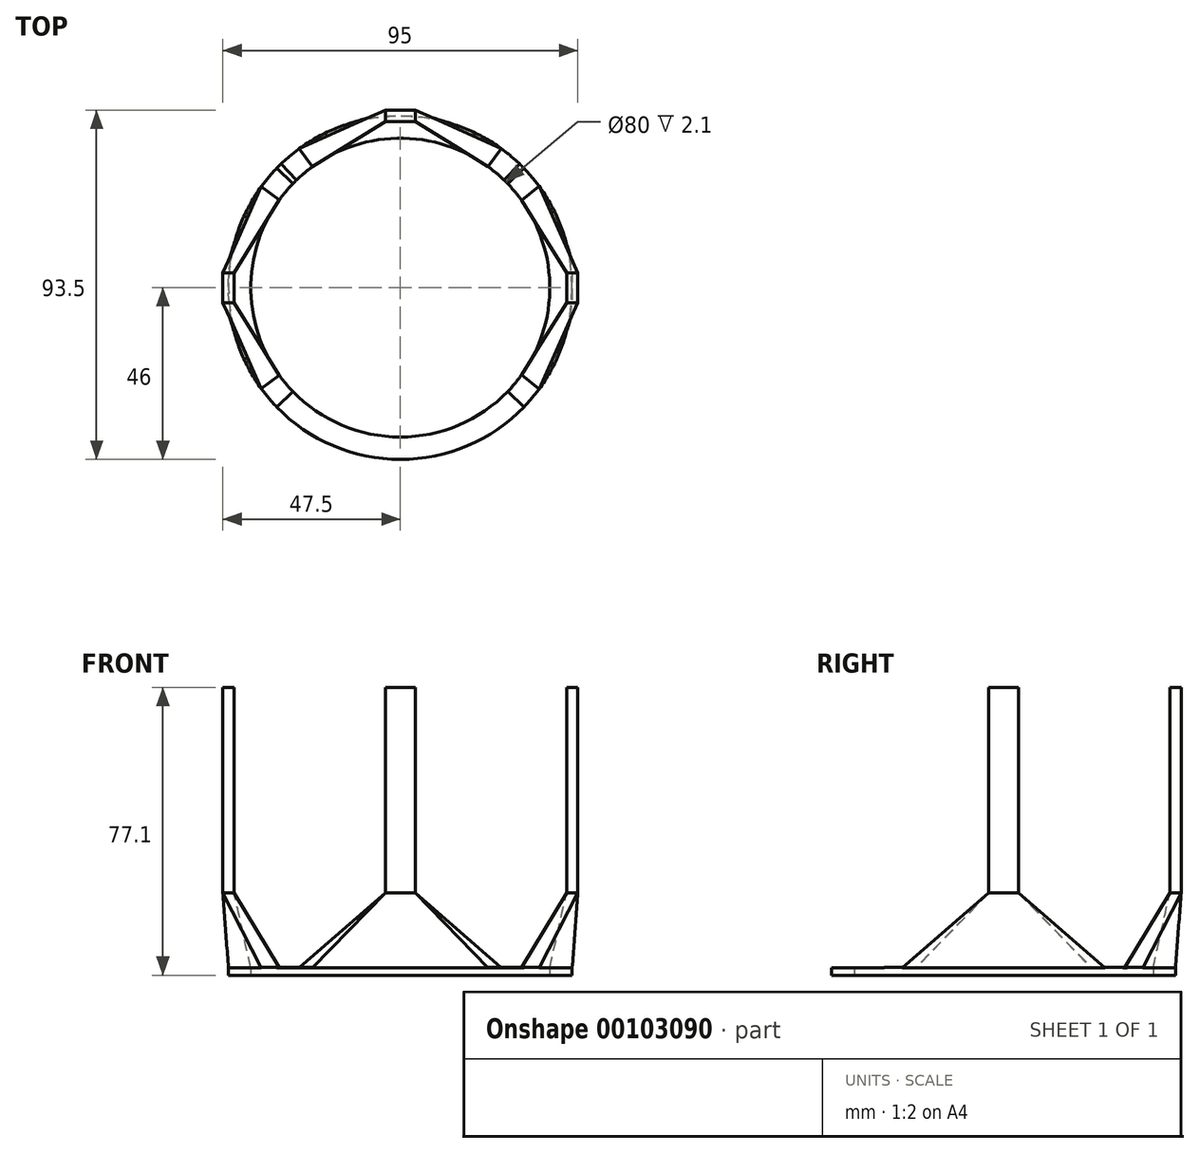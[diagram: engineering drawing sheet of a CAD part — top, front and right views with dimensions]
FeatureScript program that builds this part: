
annotation { "Feature Type Name" : "Feature", "Feature Type Description" : "" }
export const myFeature = defineFeature(function(context is Context, id is Id, definition is map)
    precondition{}
    {
        {
            var Q0;
            Q0=qCreatedBy(makeId("Top.planeOp"),FACE);
            var sketch = newSketch(context, id + "F0", { "sketchPlane" : qUnion([Q0])});
            skCircle(sketch, "E0", {"center": v(0, 0) * mm, "radius": 40 * mm});
            skCircle(sketch, "E1", {"center": v(0, 0) * mm, "radius": 46 * mm});
            skSolve(sketch);
        }
        {
            var Q0;
            Q0 = qSketchRegion(id + "F0", true);
            extrude(context, id + "F1", {"entities" : qUnion([Q0]), "depth" : 2 * mm});
        }
        {
            var Q0;
            Q0=makeQuery(id+"F1.opExtrude","CAP_FACE",FACE,{"disambiguationData":[OSD([sQuery(id+"F0.wireOp",EDGE,"E0"),sQuery(id+"F0.wireOp",EDGE,"E1")])],"isStart":false});
            var sketch = newSketch(context, id + "F2", { "sketchPlane" : qUnion([Q0])});
            skLineSegment(sketch, "E2", {"start": v(-42.45, 50.55) * mm, "end": v(44.78, -53.4) * mm, "construction": true});
            skLineSegment(sketch, "E3", {"start": v(-58.3, 48.88) * mm, "end": v(57.86, -48.58) * mm, "construction": true});
            skLineSegment(sketch, "E4", {"start": v(42.45, 50.6) * mm, "end": v(-43.35, -51.65) * mm, "construction": true});
            skLineSegment(sketch, "E5", {"start": v(-32.36, -23.51) * mm, "end": v(-37.22, -27.04) * mm});
            skLineSegment(sketch, "E6", {"start": v(-33.09, -31.95) * mm, "end": v(-28.77, -27.79) * mm});
            skPoint(sketch, "E7.endSnap0", {"position": v(-30.93, -29.87) * mm});
            skLineSegment(sketch, "E8", {"start": v(-46, 0) * mm, "end": v(-40, 0) * mm, "construction": true});
            skLineSegment(sketch, "E9", {"start": v(-33.09, 31.95) * mm, "end": v(-28.77, 27.79) * mm});
            skLineSegment(sketch, "E10", {"start": v(-37.22, 27.04) * mm, "end": v(-32.36, 23.51) * mm});
            skLineSegment(sketch, "E11", {"start": v(-30.93, 29.87) * mm, "end": v(-34.79, 25.27) * mm, "construction": true});
            skLineSegment(sketch, "E12", {"start": v(-27.04, 37.22) * mm, "end": v(-23.51, 32.36) * mm});
            skLineSegment(sketch, "E13", {"start": v(-31.95, 33.09) * mm, "end": v(-27.79, 28.77) * mm});
            skLineSegment(sketch, "E14", {"start": v(-29.87, 30.93) * mm, "end": v(-25.27, 34.79) * mm, "construction": true});
            skLineSegment(sketch, "E15", {"start": v(27.04, 37.22) * mm, "end": v(23.51, 32.36) * mm});
            skLineSegment(sketch, "E16", {"start": v(31.95, 33.1) * mm, "end": v(27.79, 28.77) * mm});
            skLineSegment(sketch, "E17", {"start": v(25.27, 34.79) * mm, "end": v(29.87, 30.93) * mm, "construction": true});
            skLineSegment(sketch, "E18", {"start": v(33.09, 31.96) * mm, "end": v(28.77, 27.79) * mm});
            skLineSegment(sketch, "E19", {"start": v(37.13, 27.15) * mm, "end": v(32.44, 23.4) * mm});
            skLineSegment(sketch, "E20", {"start": v(30.93, 29.87) * mm, "end": v(34.79, 25.28) * mm, "construction": true});
            skLineSegment(sketch, "E21", {"start": v(32.44, -23.4) * mm, "end": v(37.13, -27.15) * mm});
            skLineSegment(sketch, "E22", {"start": v(28.77, -27.79) * mm, "end": v(33.09, -31.96) * mm});
            skLineSegment(sketch, "E23", {"start": v(34.79, -25.28) * mm, "end": v(30.93, -29.87) * mm, "construction": true});
            skLineSegment(sketch, "E24", {"start": v(-30.93, -29.87) * mm, "end": v(-34.79, -25.27) * mm, "construction": true});
            skLineSegment(sketch, "E25", {"start": v(46.13, 38.7) * mm, "end": v(-50.49, -42.37) * mm, "construction": true});
            skArc(sketch, "E26.0", {"start": v(-32.36, -23.51) * mm, "mid": v(-29.26, -27.28) * mm, "end": v(-25.71, -30.64) * mm});
            skArc(sketch, "E27.0", {"start": v(-37.22, -27.04) * mm, "mid": v(-33.64, -31.37) * mm, "end": v(-29.57, -35.24) * mm});
            skArc(sketch, "E28.trimOffspring", {"start": v(-33.09, 31.95) * mm, "mid": v(-35.24, 29.57) * mm, "end": v(-37.22, 27.04) * mm});
            skArc(sketch, "E29.trimOffspring", {"start": v(-28.77, 27.79) * mm, "mid": v(-30.64, 25.71) * mm, "end": v(-32.36, 23.51) * mm});
            skArc(sketch, "E30.trimOffspring", {"start": v(-23.51, 32.36) * mm, "mid": v(-25.71, 30.64) * mm, "end": v(-27.79, 28.77) * mm});
            skArc(sketch, "E31.trimOffspring", {"start": v(-27.04, 37.22) * mm, "mid": v(-29.57, 35.24) * mm, "end": v(-31.95, 33.09) * mm});
            skArc(sketch, "E32.trimOffspring", {"start": v(31.95, 33.1) * mm, "mid": v(29.57, 35.24) * mm, "end": v(27.04, 37.22) * mm});
            skArc(sketch, "E33.trimOffspring", {"start": v(27.79, 28.77) * mm, "mid": v(25.71, 30.64) * mm, "end": v(23.51, 32.36) * mm});
            skArc(sketch, "E34.trimOffspring", {"start": v(32.44, 23.4) * mm, "mid": v(30.69, 25.66) * mm, "end": v(28.77, 27.79) * mm});
            skArc(sketch, "E35.trimOffspring", {"start": v(37.13, 27.15) * mm, "mid": v(35.2, 29.62) * mm, "end": v(33.09, 31.96) * mm});
            skArc(sketch, "E36.trimOffspring", {"start": v(28.77, -27.79) * mm, "mid": v(30.69, -25.66) * mm, "end": v(32.44, -23.4) * mm});
            skArc(sketch, "E37.trimOffspring", {"start": v(33.09, -31.96) * mm, "mid": v(35.2, -29.63) * mm, "end": v(37.13, -27.15) * mm});
            skSolve(sketch);
        }
        {
            var Q0;
            Q0 = qSketchRegion(id + "F2", true);
            extrude(context, id + "F3", {"entities" : qUnion([Q0]), "operationType" : NewBodyOperationType.ADD, "depth" : .1 * mm});
        }
        {
            var Q0;
            Q0=makeQuery(id+"F3.opExtrude","CAP_FACE",FACE,{"disambiguationData":[OSD([sQuery(id+"F2.wireOp",EDGE,"99Xpa1VF-T4qT-ukos-qWRp-hoiuqW937heV"),sQuery(id+"F2.wireOp",EDGE,"2uZg2jFw-66yj-KkDT-MyZi-Me08rNZH4T3G"),sQuery(id+"F2.wireOp",EDGE,"E5"),sQuery(id+"F2.wireOp",EDGE,"E6")])],"isStart":false});
            cPlane(context, id + "F4", {"entities" : qUnion([Q0]), "cplaneType" : CPlaneType.OFFSET, "offset" : 20 * mm, "width" : 150 * mm, "height" : 150 * mm});
        }
        {
            var Q0;
            Q0=qCreatedBy(id+"F4.planeOp",FACE);
            var sketch = newSketch(context, id + "F5", { "sketchPlane" : qUnion([Q0])});
            skLineSegment(sketch, "E38.bottom", {"start": v(-44.5, -4) * mm, "end": v(-47.5, -4) * mm});
            skLineSegment(sketch, "E38.top", {"start": v(-44.5, 4) * mm, "end": v(-47.5, 4) * mm});
            skLineSegment(sketch, "E38.left", {"start": v(-44.5, -4) * mm, "end": v(-44.5, 4) * mm});
            skLineSegment(sketch, "E38.right", {"start": v(-47.5, -4) * mm, "end": v(-47.5, 4) * mm});
            skPoint(sketch, "E38.middle", {"position": v(-46, 0) * mm});
            skCircle(sketch, "E39.0", {"center": v(0, 0) * mm, "radius": 49 * mm, "construction": true});
            skCircle(sketch, "E39.1", {"center": v(0, 0) * mm, "radius": 43 * mm, "construction": true});
            skLineSegment(sketch, "E40", {"start": v(-49, 0) * mm, "end": v(-43, 0) * mm, "construction": true});
            skLineSegment(sketch, "E41.bottom", {"start": v(4, 44.5) * mm, "end": v(-4, 44.5) * mm});
            skLineSegment(sketch, "E41.top", {"start": v(4, 47.5) * mm, "end": v(-4, 47.5) * mm});
            skLineSegment(sketch, "E41.left", {"start": v(4, 44.5) * mm, "end": v(4, 47.5) * mm});
            skLineSegment(sketch, "E41.right", {"start": v(-4, 44.5) * mm, "end": v(-4, 47.5) * mm});
            skPoint(sketch, "E41.middle", {"position": v(0, 46) * mm});
            skLineSegment(sketch, "E42", {"start": v(0, 49) * mm, "end": v(0, 43) * mm, "construction": true});
            skLineSegment(sketch, "E43", {"start": v(43, 0) * mm, "end": v(49, 0) * mm, "construction": true});
            skPoint(sketch, "E44", {"position": v(46, 0) * mm});
            skLineSegment(sketch, "E45.bottom", {"start": v(47.5, -4) * mm, "end": v(44.5, -4) * mm});
            skLineSegment(sketch, "E45.top", {"start": v(47.5, 4) * mm, "end": v(44.5, 4) * mm});
            skLineSegment(sketch, "E45.left", {"start": v(47.5, -4) * mm, "end": v(47.5, 4) * mm});
            skLineSegment(sketch, "E45.right", {"start": v(44.5, -4) * mm, "end": v(44.5, 4) * mm});
            skCircle(sketch, "E46", {"center": v(0, 0) * mm, "radius": 46 * mm, "construction": true});
            skSolve(sketch);
        }
        {
            var Q0;
            Q0 = qSketchRegion(id + "F5", true);
            extrude(context, id + "F6", {"entities" : qUnion([Q0]), "depth" : 10 * mm});
        }
        {
            var Q0;
            Q0=makeQuery(id+"F6.opExtrude","CAP_FACE",FACE,{"disambiguationData":[OSD([sQuery(id+"F5.wireOp",EDGE,"E38.bottom"),sQuery(id+"F5.wireOp",EDGE,"E38.top"),sQuery(id+"F5.wireOp",EDGE,"E38.left"),sQuery(id+"F5.wireOp",EDGE,"E38.right")])],"isStart":false});
            cPlane(context, id + "F7", {"entities" : qUnion([Q0]), "cplaneType" : CPlaneType.OFFSET, "offset" : 45 * mm, "width" : 150 * mm, "height" : 150 * mm});
        }
        {
            var Q0;
            Q0=qCreatedBy(id+"F7.planeOp",FACE);
            var sketch = newSketch(context, id + "F8", { "sketchPlane" : qUnion([Q0])});
            skLineSegment(sketch, "E47.0.0", {"start": v(-47.5, -4) * mm, "end": v(-44.5, -4) * mm});
            skLineSegment(sketch, "E47.0.1", {"start": v(-44.5, -4) * mm, "end": v(-44.5, 4) * mm});
            skLineSegment(sketch, "E47.0.2", {"start": v(-44.5, 4) * mm, "end": v(-47.5, 4) * mm});
            skLineSegment(sketch, "E47.0.3", {"start": v(-47.5, 4) * mm, "end": v(-47.5, -4) * mm});
            skLineSegment(sketch, "E48.0.0", {"start": v(44.5, -4) * mm, "end": v(47.5, -4) * mm});
            skLineSegment(sketch, "E48.0.1", {"start": v(47.5, -4) * mm, "end": v(47.5, 4) * mm});
            skLineSegment(sketch, "E48.0.2", {"start": v(47.5, 4) * mm, "end": v(44.5, 4) * mm});
            skLineSegment(sketch, "E48.0.3", {"start": v(44.5, 4) * mm, "end": v(44.5, -4) * mm});
            skLineSegment(sketch, "E49.0.0", {"start": v(-4, 44.5) * mm, "end": v(4, 44.5) * mm});
            skLineSegment(sketch, "E49.0.1", {"start": v(4, 44.5) * mm, "end": v(4, 47.5) * mm});
            skLineSegment(sketch, "E49.0.2", {"start": v(4, 47.5) * mm, "end": v(-4, 47.5) * mm});
            skLineSegment(sketch, "E49.0.3", {"start": v(-4, 47.5) * mm, "end": v(-4, 44.5) * mm});
            skSolve(sketch);
        }
        {
            var Q1;
            Q1=makeQuery(id+"F6.opExtrude","CAP_FACE",FACE,{"disambiguationData":[OSD([sQuery(id+"F5.wireOp",EDGE,"E38.bottom"),sQuery(id+"F5.wireOp",EDGE,"E38.top"),sQuery(id+"F5.wireOp",EDGE,"E38.left"),sQuery(id+"F5.wireOp",EDGE,"E38.right")])],"isStart":true});
            var Q2;
            {var subQ0=sQuery(id+"F0.wireOp",EDGE,"E0");var subQ1=sQuery(id+"F0.wireOp",EDGE,"E1");Q2=makeQuery(id+"F3.boolean.opBoolean","SPLIT",FACE,{"disambiguationData":[TD([makeQuery(id+"F3.opExtrude","SWEPT_FACE",FACE,{"disambiguationData":[OSD([sQuery(id+"F2.wireOp",EDGE,"E5")])]})])],"derivedFrom":makeQuery(id+"F1.opExtrude","CAP_FACE",FACE,{"disambiguationData":[OSD([subQ0,subQ1])],"isStart":false})});}
            loft(context, id + "F9", {"operationType" : NewBodyOperationType.ADD, "sheetProfilesArray" : [{ "sheetProfileEntities" : qUnion([Q1]) }, { "sheetProfileEntities" : qUnion([Q2]) }]});
        }
        {
            var Q1;
            Q1=makeQuery(id+"F6.opExtrude","CAP_FACE",FACE,{"disambiguationData":[OSD([sQuery(id+"F5.wireOp",EDGE,"E41.bottom"),sQuery(id+"F5.wireOp",EDGE,"E41.top"),sQuery(id+"F5.wireOp",EDGE,"E41.left"),sQuery(id+"F5.wireOp",EDGE,"E41.right")])],"isStart":true});
            var Q2;
            {var subQ0=sQuery(id+"F0.wireOp",EDGE,"E0");var subQ1=sQuery(id+"F0.wireOp",EDGE,"E1");Q2=makeQuery(id+"F3.boolean.opBoolean","SPLIT",FACE,{"disambiguationData":[TD([makeQuery(id+"F3.opExtrude","SWEPT_FACE",FACE,{"disambiguationData":[OSD([sQuery(id+"F2.wireOp",EDGE,"E12")])]})])],"derivedFrom":makeQuery(id+"F1.opExtrude","CAP_FACE",FACE,{"disambiguationData":[OSD([subQ0,subQ1])],"isStart":false})});}
            loft(context, id + "F10", {"operationType" : NewBodyOperationType.ADD, "sheetProfilesArray" : [{ "sheetProfileEntities" : qUnion([Q1]) }, { "sheetProfileEntities" : qUnion([Q2]) }]});
        }
        {
            var Q1;
            Q1=makeQuery(id+"F6.opExtrude","CAP_FACE",FACE,{"disambiguationData":[OSD([sQuery(id+"F5.wireOp",EDGE,"E45.bottom"),sQuery(id+"F5.wireOp",EDGE,"E45.top"),sQuery(id+"F5.wireOp",EDGE,"E45.left"),sQuery(id+"F5.wireOp",EDGE,"E45.right")])],"isStart":true});
            var Q2;
            {var subQ0=sQuery(id+"F0.wireOp",EDGE,"E1");var subQ1=sQuery(id+"F0.wireOp",EDGE,"E0");Q2=makeQuery(id+"F3.boolean.opBoolean","SPLIT",FACE,{"disambiguationData":[TD([makeQuery(id+"F3.opExtrude","SWEPT_FACE",FACE,{"disambiguationData":[OSD([sQuery(id+"F2.wireOp",EDGE,"E19")])]})])],"derivedFrom":makeQuery(id+"F1.opExtrude","CAP_FACE",FACE,{"disambiguationData":[OSD([subQ1,subQ0])],"isStart":false})});}
            loft(context, id + "F11", {"operationType" : NewBodyOperationType.ADD, "sheetProfilesArray" : [{ "sheetProfileEntities" : qUnion([Q1]) }, { "sheetProfileEntities" : qUnion([Q2]) }]});
        }
        {
            var Q0;
            Q0 = qSketchRegion(id + "F8", true);
            var Q1;
            Q1=makeQuery(id+"F6.opExtrude","CAP_FACE",FACE,{"disambiguationData":[OSD([sQuery(id+"F5.wireOp",EDGE,"E41.bottom"),sQuery(id+"F5.wireOp",EDGE,"E41.top"),sQuery(id+"F5.wireOp",EDGE,"E41.left"),sQuery(id+"F5.wireOp",EDGE,"E41.right")])],"isStart":false});
            extrude(context, id + "F12", {"entities" : qUnion([Q0]), "operationType" : NewBodyOperationType.ADD, "endBound" : BoundingType.UP_TO_SURFACE, "oppositeDirection" : true, "endBoundEntityFace" : qUnion([Q1]), "depth" : 25 * mm});
        }
    });
